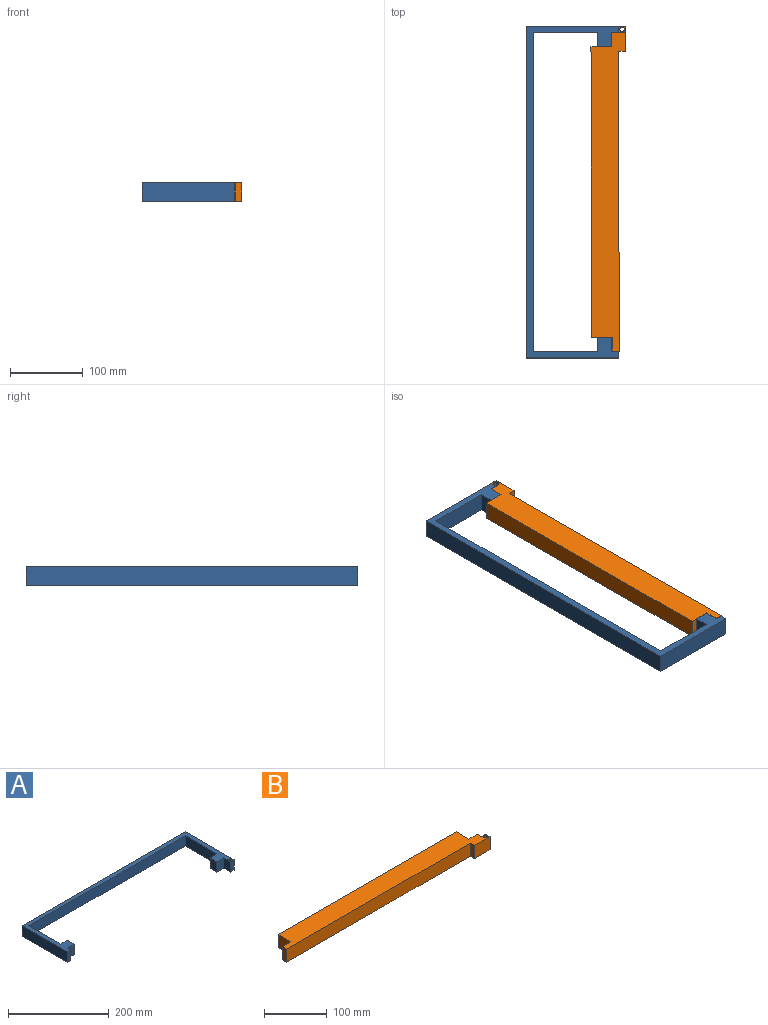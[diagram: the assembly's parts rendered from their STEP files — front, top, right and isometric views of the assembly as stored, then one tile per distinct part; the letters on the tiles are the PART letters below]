
ASSEMBLY  parts=2 mates=1
PART A: 19 faces, bbox 457.2x136.5x25.4 mm
  f0: plane 25.4x19.05mm, normal (-1,0,0), area 483.9mm2, adj f9,f10,f14,f17
  f1: plane 25.4x9.53mm, normal (1,0,0), area 241.9mm2, adj f2,f9,f10,f11
  f2: plane 25.4x9.53mm, normal (0,-1,0), area 241.9mm2, adj f1,f8,f9,f10
  f3: plane 88.9x25.4mm, normal (1,0,0), area 2258.1mm2, adj f4,f9,f10,f12
  f4: plane 438.15x25.4mm, normal (0,-1,0), area 11129mm2, adj f3,f5,f9,f10
  f5: plane 88.9x25.4mm, normal (-1,0,0), area 2258.1mm2, adj f4,f9,f10,f15
  f6: plane 136.53x25.4mm, normal (1,0,0), area 3467.7mm2, adj f7,f9,f10,f17
  f7: plane 457.2x25.4mm, normal (0,1,0), area 11612.9mm2, adj f6,f8,f9,f10
  f8: plane 127x25.4mm, normal (-1,0,0), area 3225.8mm2, adj f2,f7,f9,f10
  f9: plane 457.2x136.53mm, normal (0,0,1), area 7377.6mm2, adj f0,f1,f2,f3,f4,f5,f6,f7
  f10: plane 457.2x136.53mm, normal (0,0,-1), area 7377.6mm2, adj f0,f1,f2,f3,f4,f5,f6,f7
  f11: plane 25.4x19.05mm, normal (0,-1,0), area 483.9mm2, adj f1,f9,f10,f13
  f12: plane 25.4x19.05mm, normal (0,1,0), area 483.9mm2, adj f3,f9,f10,f13
  f13: plane 25.4x19.05mm, normal (1,0,0), area 483.9mm2, adj f9,f10,f11,f12
  f14: plane 25.4x19.05mm, normal (0,-1,0), area 483.9mm2, adj f0,f9,f10,f16
  f15: plane 25.4x19.05mm, normal (0,1,0), area 483.9mm2, adj f5,f9,f10,f16
  f16: plane 25.4x19.05mm, normal (-1,0,0), area 483.9mm2, adj f9,f10,f14,f15
  f17: plane 25.4x9.53mm, normal (0,-1,0), area 241.9mm2, adj f0,f6,f9,f10
  f18: cylinder r=3.17mm len=25.4mm, axis (0,0,1), area 506.7mm2, adj f9,f10
PART B: 15 faces, bbox 447.7x47.6x25.4 mm
  f0: plane 25.4x19.05mm, normal (0,1,0), area 483.9mm2, adj f1,f7,f8,f9
  f1: plane 28.58x25.4mm, normal (1,0,0), area 725.8mm2, adj f0,f2,f8,f9
  f2: plane 400.05x25.4mm, normal (0,1,0), area 10161.3mm2, adj f1,f3,f8,f9
  f3: plane 28.58x25.4mm, normal (-1,0,0), area 725.8mm2, adj f2,f4,f8,f9
  f4: plane 25.4x19.05mm, normal (0,1,0), area 483.9mm2, adj f3,f5,f8,f9
  f5: plane 25.4x9.53mm, normal (-1,0,0), area 241.9mm2, adj f4,f6,f8,f9
  f6: plane 412.75x25.4mm, normal (0,-1,0), area 10483.8mm2, adj f5,f8,f9,f10
  f7: plane 25.4x9.53mm, normal (1,0,0), area 241.9mm2, adj f0,f8,f9,f13
  f8: plane 447.68x47.63mm, normal (0,0,1), area 15905.8mm2, adj f0,f1,f2,f3,f4,f5,f6,f7
  f9: plane 447.68x47.63mm, normal (0,0,-1), area 15905.8mm2, adj f0,f1,f2,f3,f4,f5,f6,f7
  f10: plane 25.4x9.53mm, normal (-1,0,0), area 241.9mm2, adj f6,f8,f9,f12
  f11: plane 25.4x9.53mm, normal (1,0,0), area 241.9mm2, adj f8,f9,f12,f13
  f12: plane 34.93x25.4mm, normal (0,-1,0), area 887.1mm2, adj f8,f9,f10,f11
  f13: plane 25.4x9.53mm, normal (0,1,0), area 241.9mm2, adj f7,f8,f9,f11
  f14: cylinder r=3.17mm len=25.4mm, axis (0,0,1), area 506.7mm2, adj f8,f9
PLACE A rot(axis=(0,0,1),90deg) t=(63.5,0,-12.7)mm
PLACE B rot(axis=(0,0,1),90.1deg) t=(122.6,-0.02,-12.7)mm
MATE revolute B.f14 <-> A.f18  axis (0,0,1) through (131.75,223.84,12.7)mm
